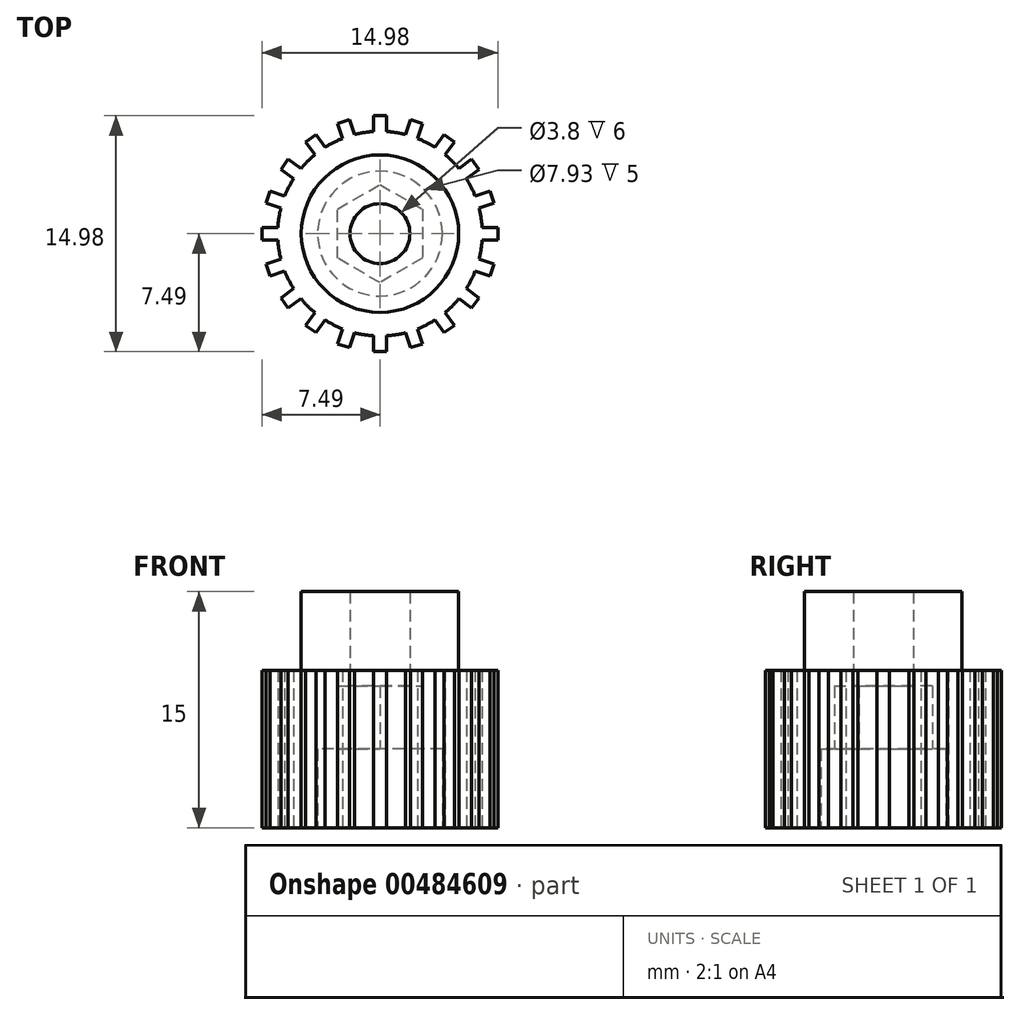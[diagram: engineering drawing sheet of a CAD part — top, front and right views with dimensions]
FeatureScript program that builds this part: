
annotation { "Feature Type Name" : "Feature", "Feature Type Description" : "" }
export const myFeature = defineFeature(function(context is Context, id is Id, definition is map)
    precondition{}
    {
        {
            var Q0;
            Q0=qCreatedBy(makeId("Top.planeOp"),FACE);
            var sketch = newSketch(context, id + "F0", { "sketchPlane" : qUnion([Q0])});
            skCircle(sketch, "E0", {"center": v(0, 0) * mm, "radius": 1.9 * mm});
            skCircle(sketch, "E1", {"center": v(0, 0) * mm, "radius": 5 * mm});
            skCircle(sketch, "E2", {"center": v(0, 0) * mm, "radius": 6.5 * mm});
            skLineSegment(sketch, "E3", {"start": v(0, 8.76) * mm, "end": v(0, -11.55) * mm, "construction": true});
            skLineSegment(sketch, "E4.bottom", {"start": v(-0.4, 7.49) * mm, "end": v(0.4, 7.49) * mm});
            skLineSegment(sketch, "E4.left", {"start": v(-0.4, 7.49) * mm, "end": v(-0.4, 6.49) * mm});
            skLineSegment(sketch, "E4.right", {"start": v(0.4, 7.49) * mm, "end": v(0.4, 6.49) * mm});
            skLineSegment(sketch, "E5.1.0", {"start": v(-2.7, 7) * mm, "end": v(-2.39, 6.05) * mm});
            skLineSegment(sketch, "E5.1.1", {"start": v(-2.7, 7) * mm, "end": v(-1.93, 7.24) * mm});
            skLineSegment(sketch, "E5.1.2", {"start": v(-1.93, 7.24) * mm, "end": v(-1.62, 6.3) * mm});
            skLineSegment(sketch, "E5.2.0", {"start": v(-4.72, 5.82) * mm, "end": v(-4.14, 5.01) * mm});
            skLineSegment(sketch, "E5.2.1", {"start": v(-4.72, 5.82) * mm, "end": v(-4.08, 6.3) * mm});
            skLineSegment(sketch, "E5.2.2", {"start": v(-4.08, 6.3) * mm, "end": v(-3.49, 5.48) * mm});
            skLineSegment(sketch, "E5.3.0", {"start": v(-6.3, 4.08) * mm, "end": v(-5.48, 3.49) * mm});
            skLineSegment(sketch, "E5.3.1", {"start": v(-6.3, 4.08) * mm, "end": v(-5.82, 4.72) * mm});
            skLineSegment(sketch, "E5.3.2", {"start": v(-5.82, 4.72) * mm, "end": v(-5.01, 4.14) * mm});
            skLineSegment(sketch, "E5.4.0", {"start": v(-7.24, 1.93) * mm, "end": v(-6.3, 1.62) * mm});
            skLineSegment(sketch, "E5.4.1", {"start": v(-7.24, 1.93) * mm, "end": v(-7, 2.7) * mm});
            skLineSegment(sketch, "E5.4.2", {"start": v(-7, 2.7) * mm, "end": v(-6.05, 2.39) * mm});
            skLineSegment(sketch, "E5.5.0", {"start": v(-7.49, -0.4) * mm, "end": v(-6.49, -0.4) * mm});
            skLineSegment(sketch, "E5.5.1", {"start": v(-7.49, -0.4) * mm, "end": v(-7.49, 0.4) * mm});
            skLineSegment(sketch, "E5.5.2", {"start": v(-7.49, 0.4) * mm, "end": v(-6.49, 0.4) * mm});
            skLineSegment(sketch, "E5.6.0", {"start": v(-7, -2.7) * mm, "end": v(-6.05, -2.39) * mm});
            skLineSegment(sketch, "E5.6.1", {"start": v(-7, -2.7) * mm, "end": v(-7.24, -1.93) * mm});
            skLineSegment(sketch, "E5.6.2", {"start": v(-7.24, -1.93) * mm, "end": v(-6.3, -1.62) * mm});
            skLineSegment(sketch, "E5.7.0", {"start": v(-5.82, -4.72) * mm, "end": v(-5.01, -4.14) * mm});
            skLineSegment(sketch, "E5.7.1", {"start": v(-5.82, -4.72) * mm, "end": v(-6.3, -4.08) * mm});
            skLineSegment(sketch, "E5.7.2", {"start": v(-6.3, -4.08) * mm, "end": v(-5.48, -3.49) * mm});
            skLineSegment(sketch, "E5.8.0", {"start": v(-4.08, -6.3) * mm, "end": v(-3.49, -5.48) * mm});
            skLineSegment(sketch, "E5.8.1", {"start": v(-4.08, -6.3) * mm, "end": v(-4.72, -5.82) * mm});
            skLineSegment(sketch, "E5.8.2", {"start": v(-4.72, -5.82) * mm, "end": v(-4.14, -5.01) * mm});
            skLineSegment(sketch, "E5.9.0", {"start": v(-1.93, -7.24) * mm, "end": v(-1.62, -6.3) * mm});
            skLineSegment(sketch, "E5.9.1", {"start": v(-1.93, -7.24) * mm, "end": v(-2.7, -7) * mm});
            skLineSegment(sketch, "E5.9.2", {"start": v(-2.7, -7) * mm, "end": v(-2.39, -6.05) * mm});
            skLineSegment(sketch, "E5.10.0", {"start": v(0.4, -7.49) * mm, "end": v(0.4, -6.49) * mm});
            skLineSegment(sketch, "E5.10.1", {"start": v(0.4, -7.49) * mm, "end": v(-0.4, -7.49) * mm});
            skLineSegment(sketch, "E5.10.2", {"start": v(-0.4, -7.49) * mm, "end": v(-0.4, -6.49) * mm});
            skLineSegment(sketch, "E5.11.0", {"start": v(2.7, -7) * mm, "end": v(2.39, -6.05) * mm});
            skLineSegment(sketch, "E5.11.1", {"start": v(2.7, -7) * mm, "end": v(1.93, -7.24) * mm});
            skLineSegment(sketch, "E5.11.2", {"start": v(1.93, -7.24) * mm, "end": v(1.62, -6.3) * mm});
            skLineSegment(sketch, "E5.12.0", {"start": v(4.72, -5.82) * mm, "end": v(4.14, -5.01) * mm});
            skLineSegment(sketch, "E5.12.1", {"start": v(4.72, -5.82) * mm, "end": v(4.08, -6.3) * mm});
            skLineSegment(sketch, "E5.12.2", {"start": v(4.08, -6.3) * mm, "end": v(3.49, -5.48) * mm});
            skLineSegment(sketch, "E5.13.0", {"start": v(6.3, -4.08) * mm, "end": v(5.48, -3.49) * mm});
            skLineSegment(sketch, "E5.13.1", {"start": v(6.3, -4.08) * mm, "end": v(5.82, -4.72) * mm});
            skLineSegment(sketch, "E5.13.2", {"start": v(5.82, -4.72) * mm, "end": v(5.01, -4.14) * mm});
            skLineSegment(sketch, "E5.14.0", {"start": v(7.24, -1.93) * mm, "end": v(6.3, -1.62) * mm});
            skLineSegment(sketch, "E5.14.1", {"start": v(7.24, -1.93) * mm, "end": v(7, -2.7) * mm});
            skLineSegment(sketch, "E5.14.2", {"start": v(7, -2.7) * mm, "end": v(6.05, -2.39) * mm});
            skLineSegment(sketch, "E5.15.0", {"start": v(7.49, 0.4) * mm, "end": v(6.49, 0.4) * mm});
            skLineSegment(sketch, "E5.15.1", {"start": v(7.49, 0.4) * mm, "end": v(7.49, -0.4) * mm});
            skLineSegment(sketch, "E5.15.2", {"start": v(7.49, -0.4) * mm, "end": v(6.49, -0.4) * mm});
            skLineSegment(sketch, "E5.16.0", {"start": v(7, 2.7) * mm, "end": v(6.05, 2.39) * mm});
            skLineSegment(sketch, "E5.16.1", {"start": v(7, 2.7) * mm, "end": v(7.24, 1.93) * mm});
            skLineSegment(sketch, "E5.16.2", {"start": v(7.24, 1.93) * mm, "end": v(6.3, 1.62) * mm});
            skLineSegment(sketch, "E5.17.0", {"start": v(5.82, 4.72) * mm, "end": v(5.01, 4.14) * mm});
            skLineSegment(sketch, "E5.17.1", {"start": v(5.82, 4.72) * mm, "end": v(6.3, 4.08) * mm});
            skLineSegment(sketch, "E5.17.2", {"start": v(6.3, 4.08) * mm, "end": v(5.48, 3.49) * mm});
            skLineSegment(sketch, "E5.18.0", {"start": v(4.08, 6.3) * mm, "end": v(3.49, 5.48) * mm});
            skLineSegment(sketch, "E5.18.1", {"start": v(4.08, 6.3) * mm, "end": v(4.72, 5.82) * mm});
            skLineSegment(sketch, "E5.18.2", {"start": v(4.72, 5.82) * mm, "end": v(4.14, 5.01) * mm});
            skLineSegment(sketch, "E5.19.0", {"start": v(1.93, 7.24) * mm, "end": v(1.62, 6.3) * mm});
            skLineSegment(sketch, "E5.19.1", {"start": v(1.93, 7.24) * mm, "end": v(2.7, 7) * mm});
            skLineSegment(sketch, "E5.19.2", {"start": v(2.7, 7) * mm, "end": v(2.39, 6.05) * mm});
            skSolve(sketch);
        }
        {
            var Q0;
            Q0=makeQuery(id+"F0.imprint","IMPRINT",FACE,{"disambiguationData":[TD([[makeQuery(id+"F0.imprint","IMPRINT",EDGE,{"derivedFrom":sQuery(id+"F0.wireOp",EDGE,"E0")}),-1.0]])]});
            extrude(context, id + "F1", {"entities" : qUnion([Q0]), "depth" : 15 * mm, "offsetDistance" : 25 * mm});
        }
        {
            var Q0;
            Q0=makeQuery(id+"F0.imprint","IMPRINT",FACE,{"disambiguationData":[TD([[makeQuery(id+"F0.imprint","IMPRINT",EDGE,{"derivedFrom":sQuery(id+"F0.wireOp",EDGE,"E1")}),-1.0]])]});
            var Q1;
            {var subQ0=sQuery(id+"F0.wireOp",EDGE,"E5.3.0");Q1=makeQuery(id+"F0.imprint","IMPRINT",FACE,{"disambiguationData":[TD([[makeQuery(id+"F0.imprint","IMPRINT",EDGE,{"derivedFrom":subQ0}),1.0]])]});}
            var Q2;
            {var subQ0=sQuery(id+"F0.wireOp",EDGE,"E5.2.0");Q2=makeQuery(id+"F0.imprint","IMPRINT",FACE,{"disambiguationData":[TD([[makeQuery(id+"F0.imprint","IMPRINT",EDGE,{"derivedFrom":subQ0}),1.0]])]});}
            var Q3;
            {var subQ0=sQuery(id+"F0.wireOp",EDGE,"E5.5.0");Q3=makeQuery(id+"F0.imprint","IMPRINT",FACE,{"disambiguationData":[TD([[makeQuery(id+"F0.imprint","IMPRINT",EDGE,{"derivedFrom":subQ0}),1.0]])]});}
            var Q4;
            {var subQ0=sQuery(id+"F0.wireOp",EDGE,"E5.6.0");Q4=makeQuery(id+"F0.imprint","IMPRINT",FACE,{"disambiguationData":[TD([[makeQuery(id+"F0.imprint","IMPRINT",EDGE,{"derivedFrom":subQ0}),1.0]])]});}
            var Q5;
            {var subQ0=sQuery(id+"F0.wireOp",EDGE,"E5.4.0");Q5=makeQuery(id+"F0.imprint","IMPRINT",FACE,{"disambiguationData":[TD([[makeQuery(id+"F0.imprint","IMPRINT",EDGE,{"derivedFrom":subQ0}),1.0]])]});}
            var Q6;
            {var subQ0=sQuery(id+"F0.wireOp",EDGE,"E5.7.0");Q6=makeQuery(id+"F0.imprint","IMPRINT",FACE,{"disambiguationData":[TD([[makeQuery(id+"F0.imprint","IMPRINT",EDGE,{"derivedFrom":subQ0}),1.0]])]});}
            var Q7;
            {var subQ0=sQuery(id+"F0.wireOp",EDGE,"E5.8.0");Q7=makeQuery(id+"F0.imprint","IMPRINT",FACE,{"disambiguationData":[TD([[makeQuery(id+"F0.imprint","IMPRINT",EDGE,{"derivedFrom":subQ0}),1.0]])]});}
            var Q8;
            {var subQ0=sQuery(id+"F0.wireOp",EDGE,"E5.9.0");Q8=makeQuery(id+"F0.imprint","IMPRINT",FACE,{"disambiguationData":[TD([[makeQuery(id+"F0.imprint","IMPRINT",EDGE,{"derivedFrom":subQ0}),1.0]])]});}
            var Q9;
            {var subQ0=sQuery(id+"F0.wireOp",EDGE,"E5.10.0");Q9=makeQuery(id+"F0.imprint","IMPRINT",FACE,{"disambiguationData":[TD([[makeQuery(id+"F0.imprint","IMPRINT",EDGE,{"derivedFrom":subQ0}),1.0]])]});}
            var Q10;
            {var subQ0=sQuery(id+"F0.wireOp",EDGE,"E5.11.0");Q10=makeQuery(id+"F0.imprint","IMPRINT",FACE,{"disambiguationData":[TD([[makeQuery(id+"F0.imprint","IMPRINT",EDGE,{"derivedFrom":subQ0}),1.0]])]});}
            var Q11;
            {var subQ0=sQuery(id+"F0.wireOp",EDGE,"E5.12.0");Q11=makeQuery(id+"F0.imprint","IMPRINT",FACE,{"disambiguationData":[TD([[makeQuery(id+"F0.imprint","IMPRINT",EDGE,{"derivedFrom":subQ0}),1.0]])]});}
            var Q12;
            {var subQ0=sQuery(id+"F0.wireOp",EDGE,"E5.14.0");Q12=makeQuery(id+"F0.imprint","IMPRINT",FACE,{"disambiguationData":[TD([[makeQuery(id+"F0.imprint","IMPRINT",EDGE,{"derivedFrom":subQ0}),1.0]])]});}
            var Q13;
            {var subQ0=sQuery(id+"F0.wireOp",EDGE,"E5.15.0");Q13=makeQuery(id+"F0.imprint","IMPRINT",FACE,{"disambiguationData":[TD([[makeQuery(id+"F0.imprint","IMPRINT",EDGE,{"derivedFrom":subQ0}),1.0]])]});}
            var Q14;
            {var subQ0=sQuery(id+"F0.wireOp",EDGE,"E5.16.0");Q14=makeQuery(id+"F0.imprint","IMPRINT",FACE,{"disambiguationData":[TD([[makeQuery(id+"F0.imprint","IMPRINT",EDGE,{"derivedFrom":subQ0}),1.0]])]});}
            var Q15;
            {var subQ0=sQuery(id+"F0.wireOp",EDGE,"E5.18.0");Q15=makeQuery(id+"F0.imprint","IMPRINT",FACE,{"disambiguationData":[TD([[makeQuery(id+"F0.imprint","IMPRINT",EDGE,{"derivedFrom":subQ0}),1.0]])]});}
            var Q16;
            {var subQ0=sQuery(id+"F0.wireOp",EDGE,"E5.13.0");Q16=makeQuery(id+"F0.imprint","IMPRINT",FACE,{"disambiguationData":[TD([[makeQuery(id+"F0.imprint","IMPRINT",EDGE,{"derivedFrom":subQ0}),1.0]])]});}
            var Q17;
            {var subQ0=sQuery(id+"F0.wireOp",EDGE,"E5.17.0");Q17=makeQuery(id+"F0.imprint","IMPRINT",FACE,{"disambiguationData":[TD([[makeQuery(id+"F0.imprint","IMPRINT",EDGE,{"derivedFrom":subQ0}),1.0]])]});}
            var Q18;
            {var subQ0=sQuery(id+"F0.wireOp",EDGE,"E5.19.0");Q18=makeQuery(id+"F0.imprint","IMPRINT",FACE,{"disambiguationData":[TD([[makeQuery(id+"F0.imprint","IMPRINT",EDGE,{"derivedFrom":subQ0}),1.0]])]});}
            var Q19;
            {var subQ0=sQuery(id+"F0.wireOp",EDGE,"E5.1.0");Q19=makeQuery(id+"F0.imprint","IMPRINT",FACE,{"disambiguationData":[TD([[makeQuery(id+"F0.imprint","IMPRINT",EDGE,{"derivedFrom":subQ0}),1.0]])]});}
            var Q20;
            Q20=makeQuery(id+"F0.imprint","IMPRINT",FACE,{"disambiguationData":[TD([[makeQuery(id+"F0.imprint","IMPRINT",EDGE,{"derivedFrom":sQuery(id+"F0.wireOp",EDGE,"E4.bottom")}),-1.0]])]});
            extrude(context, id + "F2", {"entities" : qUnion([Q0, Q1, Q2, Q3, Q4, Q5, Q6, Q7, Q8, Q9, Q10, Q11, Q12, Q13, Q14, Q15, Q16, Q17, Q18, Q19, Q20]), "operationType" : NewBodyOperationType.ADD, "depth" : 10 * mm, "offsetDistance" : 25 * mm});
        }
        {
            var Q0;
            Q0=makeQuery(id+"F0.imprint","IMPRINT",FACE,{"disambiguationData":[TD([[makeQuery(id+"F0.imprint","IMPRINT",EDGE,{"derivedFrom":sQuery(id+"F0.wireOp",EDGE,"E0")}),-1.0]])]});
            var sketch = newSketch(context, id + "F3", { "sketchPlane" : qUnion([Q0])});
            skPoint(sketch, "E6.0", {"position": v(0, 0) * mm});
            skCircle(sketch, "E7.cCircle", {"center": v(0, 0) * mm, "radius": 2.7 * mm, "construction": true});
            skLineSegment(sketch, "E7.0", {"start": v(0, 3.12) * mm, "end": v(2.7, 1.56) * mm});
            skLineSegment(sketch, "E7.1", {"start": v(2.7, 1.56) * mm, "end": v(2.7, -1.56) * mm});
            skLineSegment(sketch, "E7.2", {"start": v(2.7, -1.56) * mm, "end": v(0, -3.12) * mm});
            skLineSegment(sketch, "E7.3", {"start": v(0, -3.12) * mm, "end": v(-2.7, -1.56) * mm});
            skLineSegment(sketch, "E7.4", {"start": v(-2.7, -1.56) * mm, "end": v(-2.7, 1.56) * mm});
            skLineSegment(sketch, "E7.5", {"start": v(-2.7, 1.56) * mm, "end": v(0, 3.12) * mm});
            skPoint(sketch, "E7.0.midPoint", {"position": v(1.35, 2.34) * mm});
            skCircle(sketch, "E8", {"center": v(0, 0) * mm, "radius": 3.96 * mm});
            skSolve(sketch);
        }
        {
            var Q0;
            Q0 = qSketchRegion(id + "F3", true);
            extrude(context, id + "F4", {"entities" : qUnion([Q0]), "operationType" : NewBodyOperationType.REMOVE, "depth" : 5 * mm, "offsetDistance" : 25 * mm});
        }
        {
            var Q0;
            Q0=makeQuery(id+"F3.imprint","IMPRINT",FACE,{"disambiguationData":[TD([[makeQuery(id+"F3.imprint","IMPRINT",EDGE,{"derivedFrom":sQuery(id+"F3.wireOp",EDGE,"E7.0")}),-1.0]])]});
            extrude(context, id + "F5", {"entities" : qUnion([Q0]), "operationType" : NewBodyOperationType.REMOVE, "depth" : 9 * mm, "offsetDistance" : 25 * mm});
        }
    });
